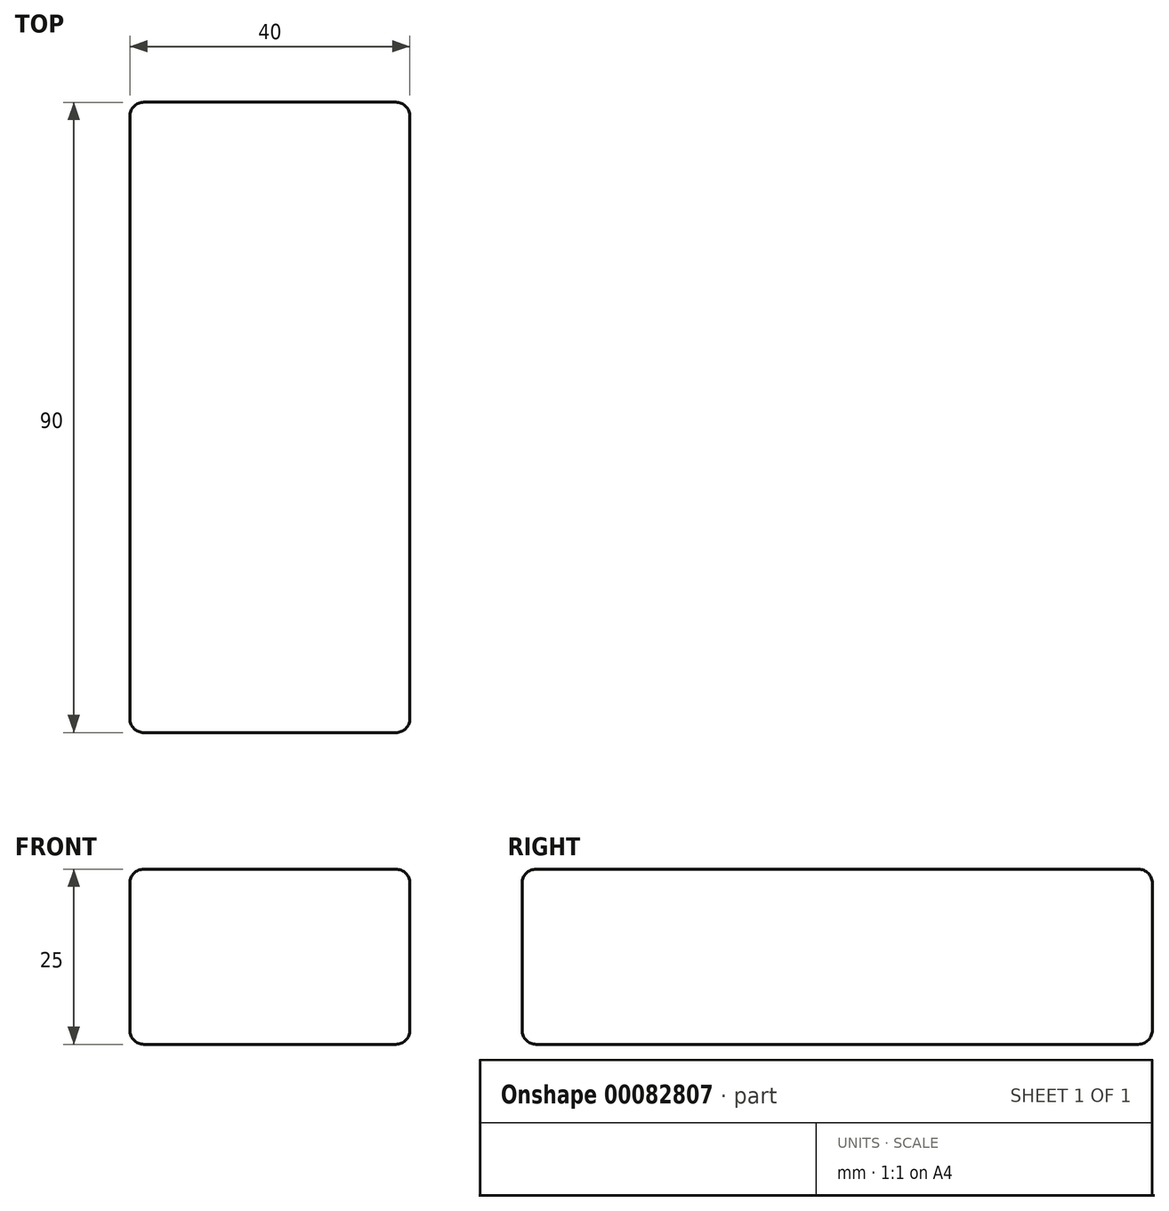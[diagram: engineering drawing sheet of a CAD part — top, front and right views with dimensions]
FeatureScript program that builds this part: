
annotation { "Feature Type Name" : "Feature", "Feature Type Description" : "" }
export const myFeature = defineFeature(function(context is Context, id is Id, definition is map)
    precondition{}
    {
        {
            var Q0;
            Q0=qCreatedBy(makeId("Top.planeOp"),FACE);
            var sketch = newSketch(context, id + "F0", { "sketchPlane" : qUnion([Q0])});
            skLineSegment(sketch, "E0.bottom", {"start": v(-25.55, 60.3) * mm, "end": v(14.45, 60.3) * mm});
            skLineSegment(sketch, "E0.top", {"start": v(-25.55, -29.7) * mm, "end": v(14.45, -29.7) * mm});
            skLineSegment(sketch, "E0.left", {"start": v(-25.55, 60.3) * mm, "end": v(-25.55, -29.7) * mm});
            skLineSegment(sketch, "E0.right", {"start": v(14.45, 60.3) * mm, "end": v(14.45, -29.7) * mm});
            skSolve(sketch);
        }
        {
            var Q0;
            Q0 = qSketchRegion(id + "F0", true);
            extrude(context, id + "F1", {"entities" : qUnion([Q0]), "depth" : 25 * mm});
        }
        {
            var Q0;
            Q0=makeQuery(id+"F1.opExtrude","CAP_FACE",FACE,{"disambiguationData":[OSD([sQuery(id+"F0.wireOp",EDGE,"E0.bottom"),sQuery(id+"F0.wireOp",EDGE,"E0.top"),sQuery(id+"F0.wireOp",EDGE,"E0.left"),sQuery(id+"F0.wireOp",EDGE,"E0.right")])],"isStart":false});
            var Q1;
            Q1=makeQuery(id+"F1.opExtrude","SWEPT_FACE",FACE,{"disambiguationData":[OSD([sQuery(id+"F0.wireOp",EDGE,"E0.left")])]});
            var Q2;
            Q2=makeQuery(id+"F1.opExtrude","SWEPT_FACE",FACE,{"disambiguationData":[OSD([sQuery(id+"F0.wireOp",EDGE,"E0.bottom")])]});
            var Q3;
            Q3=makeQuery(id+"F1.opExtrude","SWEPT_FACE",FACE,{"disambiguationData":[OSD([sQuery(id+"F0.wireOp",EDGE,"E0.right")])]});
            var Q4;
            Q4=makeQuery(id+"F1.opExtrude","CAP_FACE",FACE,{"disambiguationData":[OSD([sQuery(id+"F0.wireOp",EDGE,"E0.bottom"),sQuery(id+"F0.wireOp",EDGE,"E0.top"),sQuery(id+"F0.wireOp",EDGE,"E0.left"),sQuery(id+"F0.wireOp",EDGE,"E0.right")])],"isStart":true});
            var Q5;
            Q5=makeQuery(id+"F1.opExtrude","SWEPT_FACE",FACE,{"disambiguationData":[OSD([sQuery(id+"F0.wireOp",EDGE,"E0.top")])]});
            fillet(context, id + "F2", {"entities" : qUnion([Q0, Q1, Q2, Q3, Q4, Q5]), "radius" : 2 * mm, "tangentPropagation" : true, "allowEdgeOverflow" : false});
        }
    });
